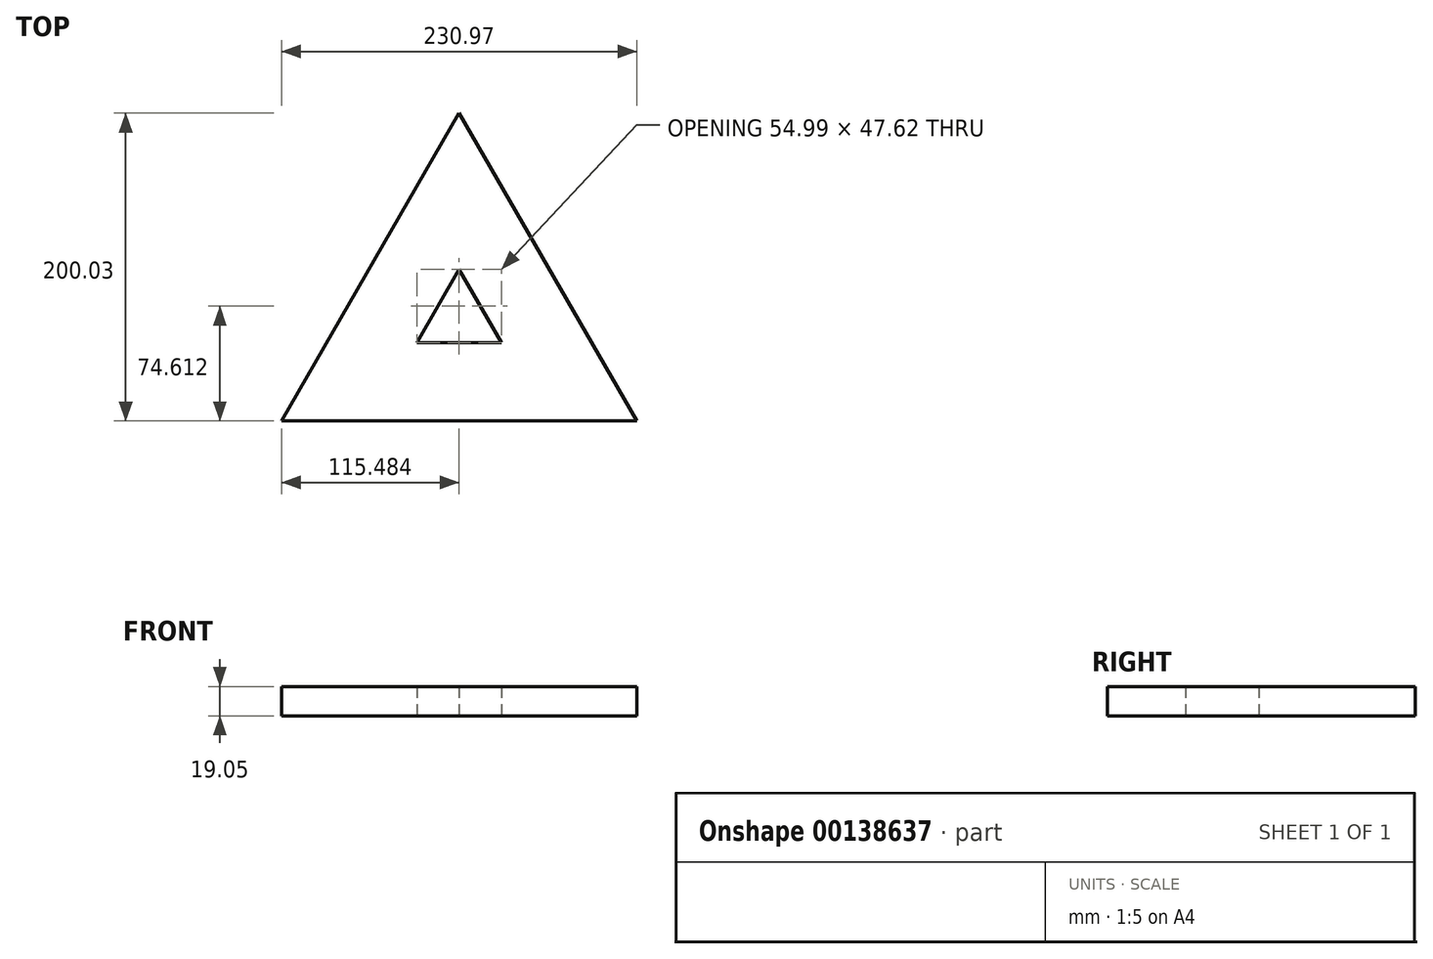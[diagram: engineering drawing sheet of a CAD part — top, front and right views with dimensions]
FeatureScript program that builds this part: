
annotation { "Feature Type Name" : "Feature", "Feature Type Description" : "" }
export const myFeature = defineFeature(function(context is Context, id is Id, definition is map)
    precondition{}
    {
        {
            var Q0;
            Q0=qCreatedBy(makeId("Top.planeOp"),FACE);
            var sketch = newSketch(context, id + "F0", { "sketchPlane" : qUnion([Q0])});
            skLineSegment(sketch, "E0", {"start": v(0, 0) * mm, "end": v(230.97, 0) * mm});
            skLineSegment(sketch, "E1", {"start": v(0, 0) * mm, "end": v(115.48, 200.02) * mm});
            skLineSegment(sketch, "E2", {"start": v(230.97, 0) * mm, "end": v(115.48, 200.02) * mm});
            skLineSegment(sketch, "E3", {"start": v(115.48, 0) * mm, "end": v(115.48, 66.67) * mm, "construction": true});
            skLineSegment(sketch, "E4", {"start": v(57.74, 100.01) * mm, "end": v(115.48, 66.67) * mm, "construction": true});
            skLineSegment(sketch, "E5", {"start": v(115.48, 66.67) * mm, "end": v(173.23, 100.01) * mm, "construction": true});
            skCircle(sketch, "E6", {"center": v(115.48, 66.67) * mm, "radius": 15.88 * mm});
            skLineSegment(sketch, "E7", {"start": v(142.98, 0) * mm, "end": v(142.98, 50.8) * mm, "construction": true});
            skLineSegment(sketch, "E8", {"start": v(142.98, 50.8) * mm, "end": v(87.99, 50.8) * mm});
            skLineSegment(sketch, "E9", {"start": v(159.48, 123.82) * mm, "end": v(115.48, 98.42) * mm, "construction": true});
            skLineSegment(sketch, "E10", {"start": v(71.5, 123.82) * mm, "end": v(115.48, 98.42) * mm, "construction": true});
            skLineSegment(sketch, "E11", {"start": v(115.48, 98.42) * mm, "end": v(142.98, 50.8) * mm});
            skLineSegment(sketch, "E12", {"start": v(115.48, 98.42) * mm, "end": v(87.99, 50.8) * mm});
            skSolve(sketch);
        }
        {
            var Q0;
            Q0=makeQuery(id+"F0.imprint","IMPRINT",FACE,{"disambiguationData":[TD([[makeQuery(id+"F0.imprint","IMPRINT",EDGE,{"derivedFrom":sQuery(id+"F0.wireOp",EDGE,"E0")}),1.0]])]});
            extrude(context, id + "F1", {"entities" : qUnion([Q0]), "depth" : 19.05 * mm});
        }
    });
